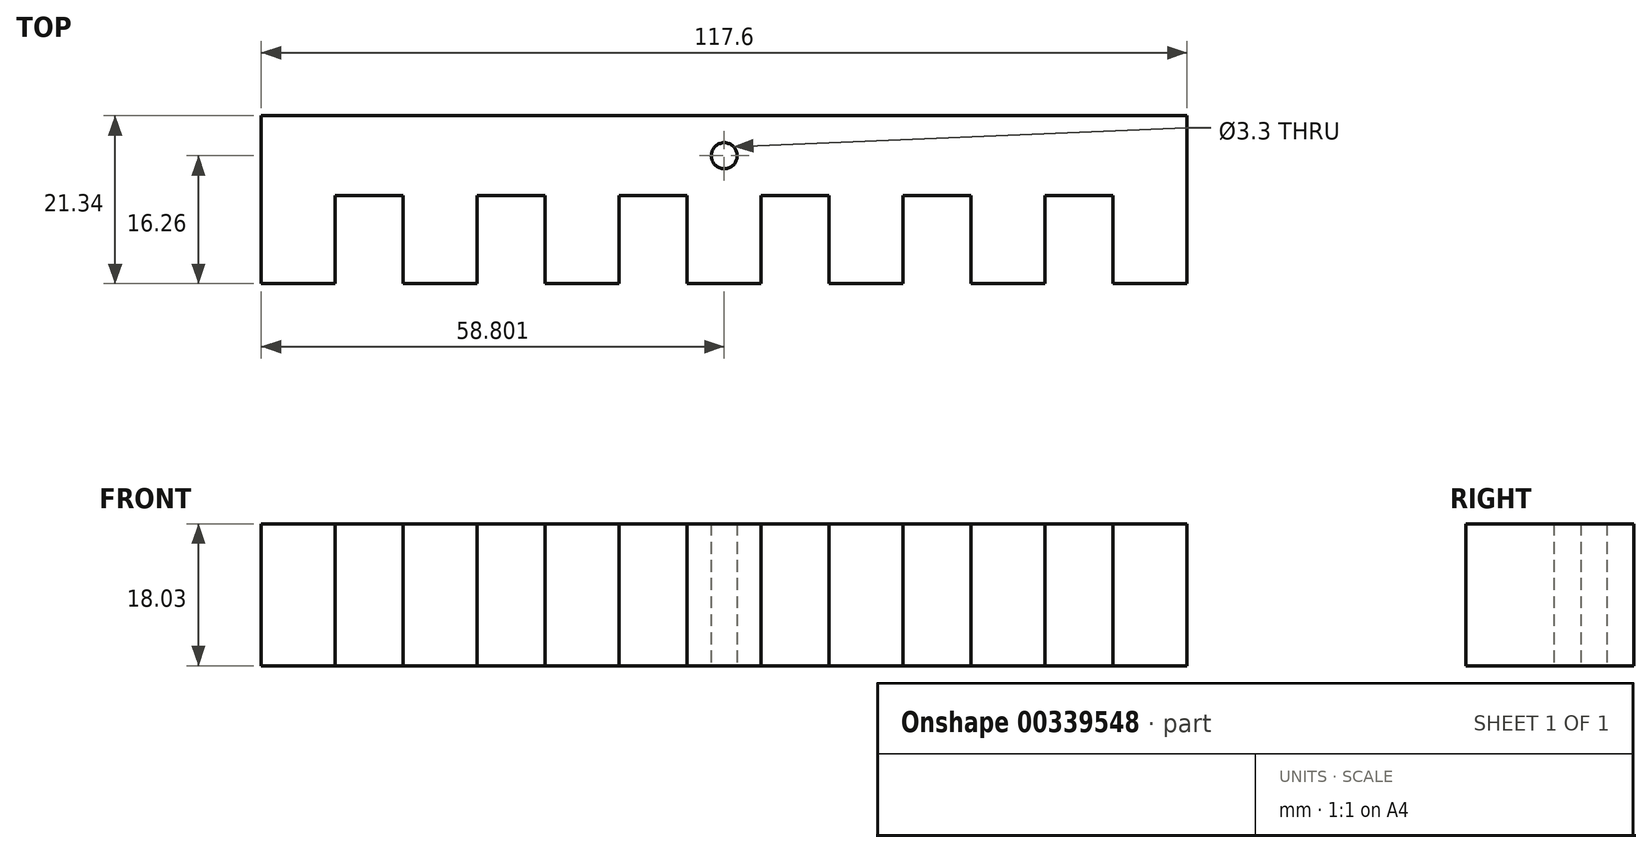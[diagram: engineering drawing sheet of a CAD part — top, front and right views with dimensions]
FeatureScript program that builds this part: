
annotation { "Feature Type Name" : "Feature", "Feature Type Description" : "" }
export const myFeature = defineFeature(function(context is Context, id is Id, definition is map)
    precondition{}
    {
        {
            var Q0;
            Q0=qCreatedBy(makeId("Top.planeOp"),FACE);
            var sketch = newSketch(context, id + "F0", { "sketchPlane" : qUnion([Q0])});
            skLineSegment(sketch, "E0", {"start": v(-47, 0) * mm, "end": v(-47, -21.34) * mm});
            skLineSegment(sketch, "E1", {"start": v(-47, -21.34) * mm, "end": v(-37.6, -21.34) * mm});
            skLineSegment(sketch, "E2", {"start": v(-37.6, -21.34) * mm, "end": v(-37.6, -10.16) * mm});
            skLineSegment(sketch, "E3", {"start": v(-37.6, -10.16) * mm, "end": v(-28.96, -10.16) * mm});
            skLineSegment(sketch, "E4", {"start": v(-28.96, -10.16) * mm, "end": v(-28.96, -21.34) * mm});
            skLineSegment(sketch, "E5", {"start": v(-28.96, -21.34) * mm, "end": v(-19.56, -21.34) * mm});
            skLineSegment(sketch, "E6", {"start": v(-19.56, -21.34) * mm, "end": v(-19.56, -10.16) * mm});
            skLineSegment(sketch, "E7", {"start": v(-19.56, -10.16) * mm, "end": v(-10.92, -10.16) * mm});
            skLineSegment(sketch, "E8", {"start": v(-10.92, -10.16) * mm, "end": v(-10.92, -21.34) * mm});
            skLineSegment(sketch, "E9", {"start": v(-10.92, -21.34) * mm, "end": v(-1.52, -21.34) * mm});
            skLineSegment(sketch, "E10", {"start": v(-1.52, -21.34) * mm, "end": v(-1.52, -10.16) * mm});
            skLineSegment(sketch, "E11", {"start": v(-1.52, -10.16) * mm, "end": v(7.11, -10.16) * mm});
            skLineSegment(sketch, "E12", {"start": v(7.11, -10.16) * mm, "end": v(7.11, -21.34) * mm});
            skLineSegment(sketch, "E13", {"start": v(7.11, -21.34) * mm, "end": v(16.5, -21.34) * mm});
            skLineSegment(sketch, "E14", {"start": v(16.5, -21.34) * mm, "end": v(16.5, -10.16) * mm});
            skLineSegment(sketch, "E15", {"start": v(16.5, -10.16) * mm, "end": v(25.15, -10.16) * mm});
            skLineSegment(sketch, "E16", {"start": v(25.15, -10.16) * mm, "end": v(25.15, -21.34) * mm});
            skLineSegment(sketch, "E17", {"start": v(25.15, -21.34) * mm, "end": v(34.54, -21.34) * mm});
            skLineSegment(sketch, "E18", {"start": v(34.54, -21.34) * mm, "end": v(34.54, -10.16) * mm});
            skLineSegment(sketch, "E19", {"start": v(34.54, -10.16) * mm, "end": v(43.18, -10.16) * mm});
            skLineSegment(sketch, "E20", {"start": v(43.18, -10.16) * mm, "end": v(43.18, -21.34) * mm});
            skLineSegment(sketch, "E21", {"start": v(43.18, -21.34) * mm, "end": v(52.58, -21.34) * mm});
            skLineSegment(sketch, "E22", {"start": v(52.58, -21.34) * mm, "end": v(52.58, -10.16) * mm});
            skLineSegment(sketch, "E23", {"start": v(52.58, -10.16) * mm, "end": v(61.21, -10.16) * mm});
            skLineSegment(sketch, "E24", {"start": v(61.21, -10.16) * mm, "end": v(61.21, -21.34) * mm});
            skLineSegment(sketch, "E25", {"start": v(61.21, -21.34) * mm, "end": v(70.61, -21.34) * mm});
            skLineSegment(sketch, "E26", {"start": v(70.61, -21.34) * mm, "end": v(70.61, 0) * mm});
            skLineSegment(sketch, "E27", {"start": v(70.61, 0) * mm, "end": v(-47, 0) * mm});
            skCircle(sketch, "E28", {"center": v(11.81, -5.08) * mm, "radius": 1.65 * mm});
            skSolve(sketch);
        }
        {
            var Q0;
            Q0 = qSketchRegion(id + "F0", true);
            extrude(context, id + "F1", {"entities" : qUnion([Q0]), "depth" : 18.03 * mm});
        }
    });
